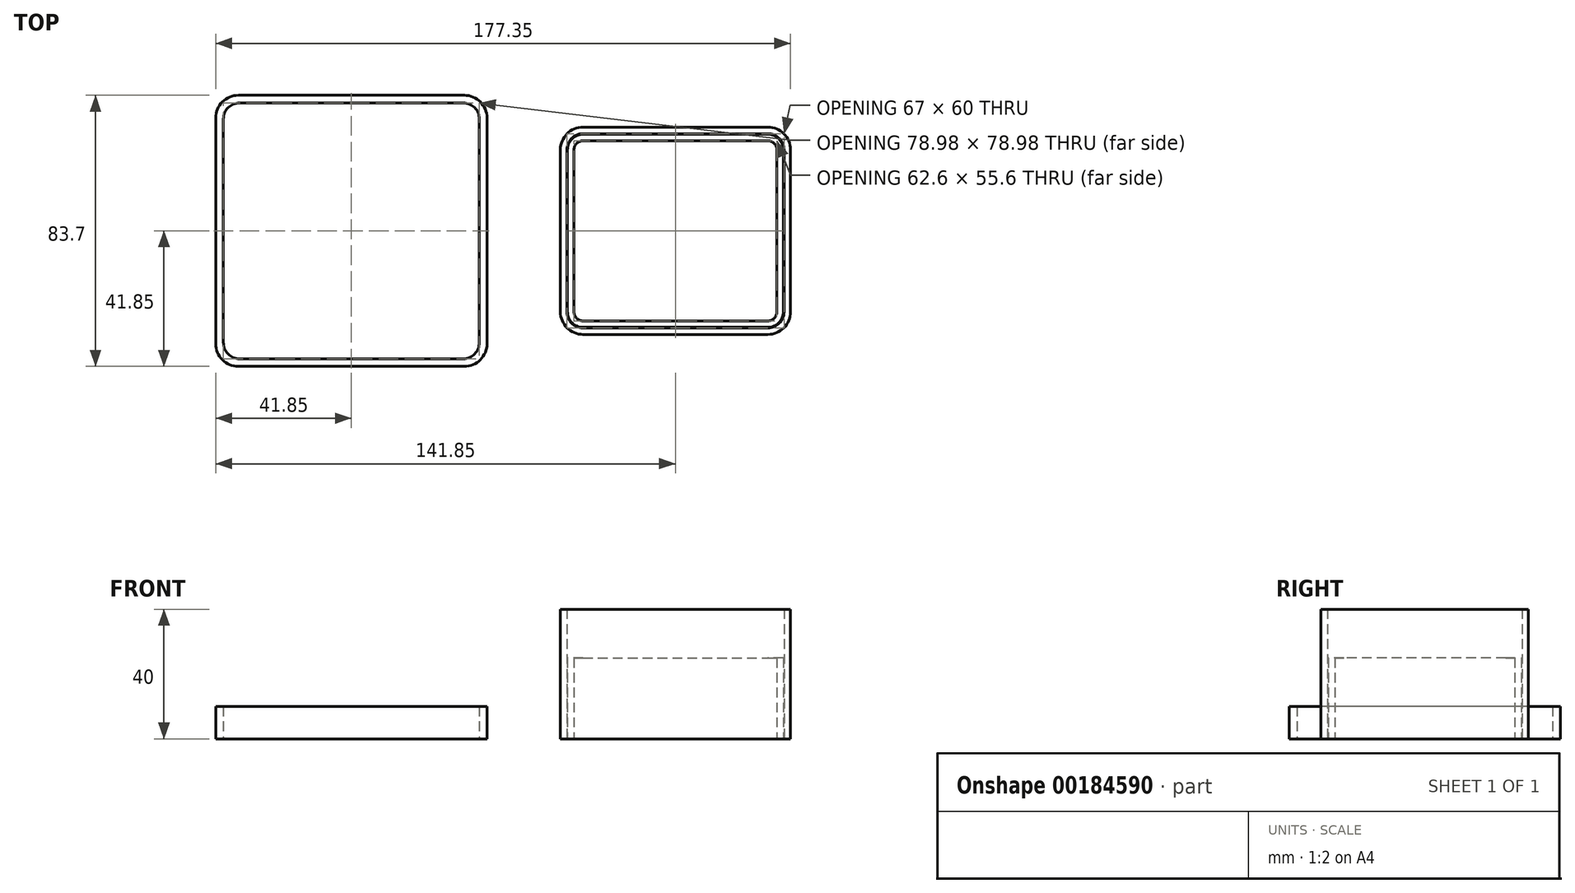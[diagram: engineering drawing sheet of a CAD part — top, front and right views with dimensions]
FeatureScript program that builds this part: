
annotation { "Feature Type Name" : "Feature", "Feature Type Description" : "" }
export const myFeature = defineFeature(function(context is Context, id is Id, definition is map)
    precondition{}
    {
        {
            var Q0;
            Q0=qCreatedBy(makeId("Top.planeOp"),FACE);
            var sketch = newSketch(context, id + "F0", { "sketchPlane" : qUnion([Q0])});
            skLineSegment(sketch, "E0.bottom", {"start": v(-28.5, 32) * mm, "end": v(28.5, 32) * mm});
            skLineSegment(sketch, "E0.top", {"start": v(-28.5, -32) * mm, "end": v(28.5, -32) * mm});
            skLineSegment(sketch, "E0.left", {"start": v(-35.5, 25) * mm, "end": v(-35.5, -25) * mm});
            skLineSegment(sketch, "E0.right", {"start": v(35.5, 25) * mm, "end": v(35.5, -25) * mm});
            skPoint(sketch, "E0.middle", {"position": v(0, 0) * mm});
            skLineSegment(sketch, "E1.0", {"start": v(-28.5, 30) * mm, "end": v(28.5, 30) * mm});
            skLineSegment(sketch, "E1.1", {"start": v(-33.5, 25) * mm, "end": v(-33.5, -25) * mm});
            skLineSegment(sketch, "E1.2", {"start": v(-28.5, -30) * mm, "end": v(28.5, -30) * mm});
            skLineSegment(sketch, "E1.3", {"start": v(33.5, 25) * mm, "end": v(33.5, -25) * mm});
            skLineSegment(sketch, "E2.0", {"start": v(-28.5, 29.8) * mm, "end": v(28.5, 29.8) * mm});
            skLineSegment(sketch, "E2.1", {"start": v(-33.3, 25) * mm, "end": v(-33.3, -25) * mm});
            skLineSegment(sketch, "E2.2", {"start": v(-28.5, -29.8) * mm, "end": v(28.5, -29.8) * mm});
            skLineSegment(sketch, "E2.3", {"start": v(33.3, 25) * mm, "end": v(33.3, -25) * mm});
            skLineSegment(sketch, "E3.0", {"start": v(-28.5, 27.8) * mm, "end": v(28.5, 27.8) * mm});
            skLineSegment(sketch, "E3.1", {"start": v(-31.3, 25) * mm, "end": v(-31.3, -25) * mm});
            skLineSegment(sketch, "E3.2", {"start": v(-28.5, -27.8) * mm, "end": v(28.5, -27.8) * mm});
            skLineSegment(sketch, "E3.3", {"start": v(31.3, 25) * mm, "end": v(31.3, -25) * mm});
            skPoint(sketch, "E4.visualSharp", {"position": v(-35.5, 32) * mm});
            skArc(sketch, "E4.filletArc", {"start": v(-28.5, 32) * mm, "mid": v(-33.45, 29.95) * mm, "end": v(-35.5, 25) * mm});
            skPoint(sketch, "E5.visualSharp", {"position": v(-35.5, -32) * mm});
            skArc(sketch, "E5.filletArc", {"start": v(-35.5, -25) * mm, "mid": v(-33.45, -29.95) * mm, "end": v(-28.5, -32) * mm});
            skPoint(sketch, "E6.visualSharp", {"position": v(35.5, -32) * mm});
            skArc(sketch, "E6.filletArc", {"start": v(28.5, -32) * mm, "mid": v(33.45, -29.95) * mm, "end": v(35.5, -25) * mm});
            skPoint(sketch, "E7.visualSharp", {"position": v(35.5, 32) * mm});
            skArc(sketch, "E7.filletArc", {"start": v(35.5, 25) * mm, "mid": v(33.45, 29.95) * mm, "end": v(28.5, 32) * mm});
            skPoint(sketch, "E8.visualSharp", {"position": v(-33.5, 30) * mm});
            skArc(sketch, "E8.filletArc", {"start": v(-28.5, 30) * mm, "mid": v(-32.04, 28.54) * mm, "end": v(-33.5, 25) * mm});
            skPoint(sketch, "E9.visualSharp", {"position": v(-33.5, -30) * mm});
            skArc(sketch, "E9.filletArc", {"start": v(-33.5, -25) * mm, "mid": v(-32.04, -28.54) * mm, "end": v(-28.5, -30) * mm});
            skPoint(sketch, "E10.visualSharp", {"position": v(33.5, -30) * mm});
            skArc(sketch, "E10.filletArc", {"start": v(28.5, -30) * mm, "mid": v(32.04, -28.54) * mm, "end": v(33.5, -25) * mm});
            skPoint(sketch, "E11.visualSharp", {"position": v(33.5, 30) * mm});
            skArc(sketch, "E11.filletArc", {"start": v(33.5, 25) * mm, "mid": v(32.04, 28.54) * mm, "end": v(28.5, 30) * mm});
            skPoint(sketch, "E12.visualSharp", {"position": v(-33.3, 29.8) * mm});
            skArc(sketch, "E12.filletArc", {"start": v(-28.5, 29.8) * mm, "mid": v(-31.9, 28.4) * mm, "end": v(-33.3, 25) * mm});
            skPoint(sketch, "E13.visualSharp", {"position": v(33.3, 29.8) * mm});
            skArc(sketch, "E13.filletArc", {"start": v(33.3, 25) * mm, "mid": v(31.9, 28.4) * mm, "end": v(28.5, 29.8) * mm});
            skPoint(sketch, "E14.visualSharp", {"position": v(33.3, -29.8) * mm});
            skArc(sketch, "E14.filletArc", {"start": v(28.5, -29.8) * mm, "mid": v(31.9, -28.4) * mm, "end": v(33.3, -25) * mm});
            skPoint(sketch, "E15.visualSharp", {"position": v(-33.3, -29.8) * mm});
            skArc(sketch, "E15.filletArc", {"start": v(-33.3, -25) * mm, "mid": v(-31.9, -28.4) * mm, "end": v(-28.5, -29.8) * mm});
            skPoint(sketch, "E16.visualSharp", {"position": v(31.3, 27.8) * mm});
            skArc(sketch, "E16.filletArc", {"start": v(31.3, 25) * mm, "mid": v(30.48, 26.98) * mm, "end": v(28.5, 27.8) * mm});
            skPoint(sketch, "E17.visualSharp", {"position": v(31.3, -27.8) * mm});
            skArc(sketch, "E17.filletArc", {"start": v(28.5, -27.8) * mm, "mid": v(30.48, -26.98) * mm, "end": v(31.3, -25) * mm});
            skPoint(sketch, "E18.visualSharp", {"position": v(-31.3, -27.8) * mm});
            skArc(sketch, "E18.filletArc", {"start": v(-31.3, -25) * mm, "mid": v(-30.48, -26.98) * mm, "end": v(-28.5, -27.8) * mm});
            skPoint(sketch, "E19.visualSharp", {"position": v(-31.3, 27.8) * mm});
            skArc(sketch, "E19.filletArc", {"start": v(-28.5, 27.8) * mm, "mid": v(-30.48, 26.98) * mm, "end": v(-31.3, 25) * mm});
            skSolve(sketch);
        }
        {
            var Q0;
            Q0=makeQuery(id+"F0.imprint","IMPRINT",FACE,{"disambiguationData":[TD([[makeQuery(id+"F0.imprint","IMPRINT",EDGE,{"derivedFrom":sQuery(id+"F0.wireOp",EDGE,"E2.0")}),-1.0]])]});
            extrude(context, id + "F1", {"entities" : qUnion([Q0]), "depth" : 25 * mm});
        }
        {
            var Q0;
            Q0=makeQuery(id+"F0.imprint","IMPRINT",FACE,{"disambiguationData":[TD([[makeQuery(id+"F0.imprint","IMPRINT",EDGE,{"derivedFrom":sQuery(id+"F0.wireOp",EDGE,"E0.bottom")}),-1.0]])]});
            extrude(context, id + "F2", {"entities" : qUnion([Q0]), "depth" : 40 * mm});
        }
        {
            var Q0;
            Q0=qCreatedBy(makeId("Top.planeOp"),FACE);
            var sketch = newSketch(context, id + "F3", { "sketchPlane" : qUnion([Q0])});
            skLineSegment(sketch, "E20.bottom", {"start": v(-134.85, 41.85) * mm, "end": v(-65.15, 41.85) * mm});
            skLineSegment(sketch, "E20.top", {"start": v(-134.85, -41.85) * mm, "end": v(-65.15, -41.85) * mm});
            skLineSegment(sketch, "E20.left", {"start": v(-141.85, 34.85) * mm, "end": v(-141.85, -34.85) * mm});
            skLineSegment(sketch, "E20.right", {"start": v(-58.15, 34.85) * mm, "end": v(-58.15, -34.85) * mm});
            skPoint(sketch, "E20.middle", {"position": v(-100, 0) * mm});
            skLineSegment(sketch, "E21.0", {"start": v(-134.5, 39.5) * mm, "end": v(-65.51, 39.5) * mm});
            skLineSegment(sketch, "E21.1", {"start": v(-139.5, 34.5) * mm, "end": v(-139.5, -34.49) * mm});
            skLineSegment(sketch, "E21.2", {"start": v(-134.5, -39.49) * mm, "end": v(-65.51, -39.49) * mm});
            skLineSegment(sketch, "E21.3", {"start": v(-60.5, 34.5) * mm, "end": v(-60.5, -34.49) * mm});
            skLineSegment(sketch, "E22.0", {"start": v(-134.5, 39.3) * mm, "end": v(-65.51, 39.3) * mm});
            skLineSegment(sketch, "E22.1", {"start": v(-139.29, 34.5) * mm, "end": v(-139.29, -34.49) * mm});
            skLineSegment(sketch, "E22.2", {"start": v(-134.5, -39.29) * mm, "end": v(-65.51, -39.29) * mm});
            skLineSegment(sketch, "E22.3", {"start": v(-60.7, 34.5) * mm, "end": v(-60.7, -34.49) * mm});
            skLineSegment(sketch, "E23.0", {"start": v(-134.5, 37.3) * mm, "end": v(-65.5, 37.3) * mm});
            skLineSegment(sketch, "E23.1", {"start": v(-137.29, 34.5) * mm, "end": v(-137.29, -34.49) * mm});
            skLineSegment(sketch, "E23.2", {"start": v(-134.5, -37.29) * mm, "end": v(-65.5, -37.29) * mm});
            skLineSegment(sketch, "E23.3", {"start": v(-62.7, 34.5) * mm, "end": v(-62.7, -34.49) * mm});
            skPoint(sketch, "E24.visualSharp", {"position": v(-141.85, 41.85) * mm});
            skArc(sketch, "E24.filletArc", {"start": v(-134.85, 41.85) * mm, "mid": v(-139.8, 39.8) * mm, "end": v(-141.85, 34.85) * mm});
            skPoint(sketch, "E25.visualSharp", {"position": v(-141.85, -41.85) * mm});
            skArc(sketch, "E25.filletArc", {"start": v(-141.85, -34.85) * mm, "mid": v(-139.8, -39.8) * mm, "end": v(-134.85, -41.85) * mm});
            skPoint(sketch, "E26.visualSharp", {"position": v(-58.15, -41.85) * mm});
            skArc(sketch, "E26.filletArc", {"start": v(-65.15, -41.85) * mm, "mid": v(-60.2, -39.8) * mm, "end": v(-58.15, -34.85) * mm});
            skPoint(sketch, "E27.visualSharp", {"position": v(-58.15, 41.85) * mm});
            skArc(sketch, "E27.filletArc", {"start": v(-58.15, 34.85) * mm, "mid": v(-60.2, 39.8) * mm, "end": v(-65.15, 41.85) * mm});
            skPoint(sketch, "E28.visualSharp", {"position": v(-139.5, 39.5) * mm});
            skArc(sketch, "E28.filletArc", {"start": v(-134.5, 39.5) * mm, "mid": v(-138.03, 38.03) * mm, "end": v(-139.5, 34.5) * mm});
            skPoint(sketch, "E29.visualSharp", {"position": v(-139.5, -39.49) * mm});
            skArc(sketch, "E29.filletArc", {"start": v(-139.5, -34.49) * mm, "mid": v(-138.03, -38.03) * mm, "end": v(-134.5, -39.49) * mm});
            skPoint(sketch, "E30.visualSharp", {"position": v(-60.5, -39.49) * mm});
            skArc(sketch, "E30.filletArc", {"start": v(-65.51, -39.49) * mm, "mid": v(-61.97, -38.03) * mm, "end": v(-60.5, -34.49) * mm});
            skPoint(sketch, "E31.visualSharp", {"position": v(-60.5, 39.5) * mm});
            skArc(sketch, "E31.filletArc", {"start": v(-60.5, 34.5) * mm, "mid": v(-61.97, 38.03) * mm, "end": v(-65.51, 39.5) * mm});
            skPoint(sketch, "E32.visualSharp", {"position": v(-139.29, 39.3) * mm});
            skArc(sketch, "E32.filletArc", {"start": v(-134.5, 39.3) * mm, "mid": v(-137.88, 37.88) * mm, "end": v(-139.29, 34.5) * mm});
            skPoint(sketch, "E33.visualSharp", {"position": v(-60.7, 39.3) * mm});
            skArc(sketch, "E33.filletArc", {"start": v(-60.7, 34.5) * mm, "mid": v(-62.12, 37.88) * mm, "end": v(-65.51, 39.3) * mm});
            skPoint(sketch, "E34.visualSharp", {"position": v(-60.7, -39.29) * mm});
            skArc(sketch, "E34.filletArc", {"start": v(-65.51, -39.29) * mm, "mid": v(-62.12, -37.88) * mm, "end": v(-60.7, -34.49) * mm});
            skPoint(sketch, "E35.visualSharp", {"position": v(-139.29, -39.29) * mm});
            skArc(sketch, "E35.filletArc", {"start": v(-139.29, -34.49) * mm, "mid": v(-137.88, -37.88) * mm, "end": v(-134.5, -39.29) * mm});
            skPoint(sketch, "E36.visualSharp", {"position": v(-62.7, 37.3) * mm});
            skArc(sketch, "E36.filletArc", {"start": v(-62.7, 34.5) * mm, "mid": v(-63.53, 36.47) * mm, "end": v(-65.5, 37.3) * mm});
            skPoint(sketch, "E37.visualSharp", {"position": v(-62.7, -37.29) * mm});
            skArc(sketch, "E37.filletArc", {"start": v(-65.5, -37.29) * mm, "mid": v(-63.53, -36.47) * mm, "end": v(-62.7, -34.49) * mm});
            skPoint(sketch, "E38.visualSharp", {"position": v(-137.29, -37.29) * mm});
            skArc(sketch, "E38.filletArc", {"start": v(-137.29, -34.49) * mm, "mid": v(-136.47, -36.47) * mm, "end": v(-134.5, -37.29) * mm});
            skPoint(sketch, "E39.visualSharp", {"position": v(-137.29, 37.3) * mm});
            skArc(sketch, "E39.filletArc", {"start": v(-134.5, 37.3) * mm, "mid": v(-136.47, 36.47) * mm, "end": v(-137.29, 34.5) * mm});
            skSolve(sketch);
        }
        {
            var Q0;
            Q0=makeQuery(id+"F3.imprint","IMPRINT",FACE,{"disambiguationData":[TD([[makeQuery(id+"F3.imprint","IMPRINT",EDGE,{"derivedFrom":sQuery(id+"F3.wireOp",EDGE,"E20.bottom")}),-1.0]])]});
            extrude(context, id + "F4", {"entities" : qUnion([Q0]), "depth" : 10 * mm});
        }
    });
